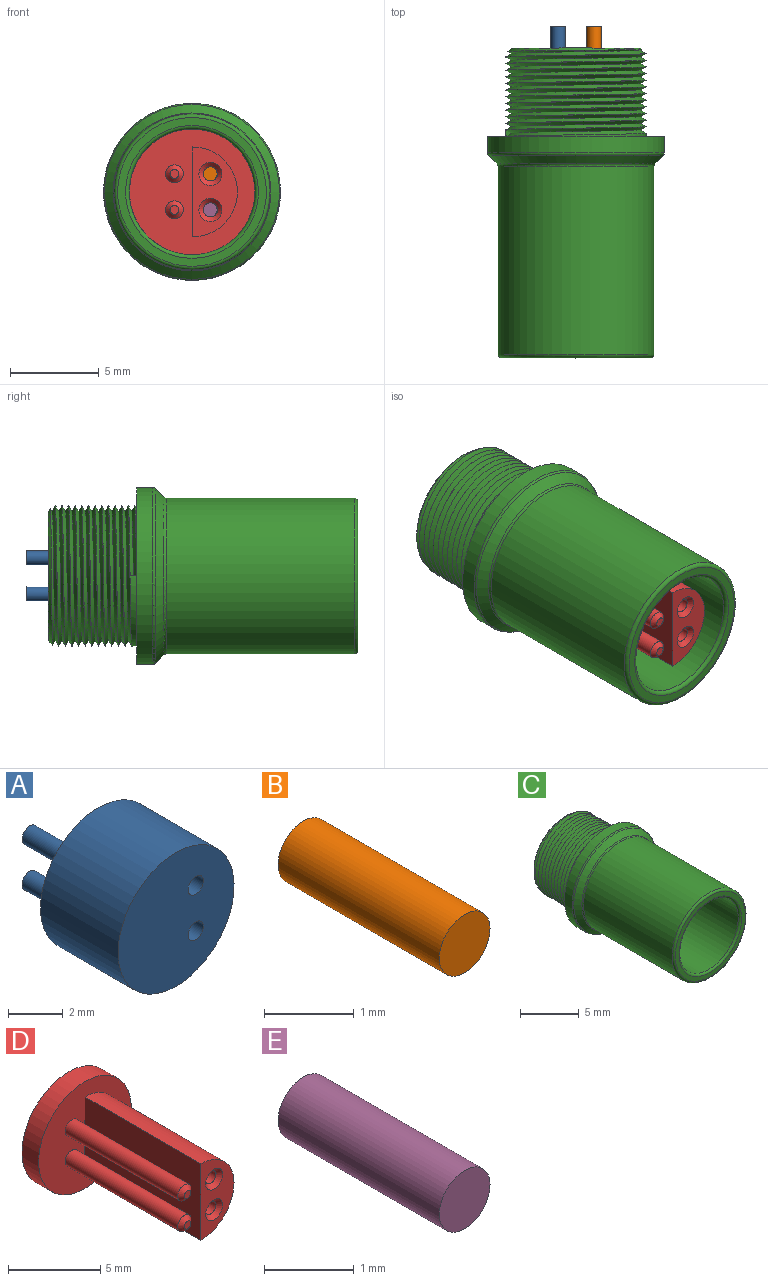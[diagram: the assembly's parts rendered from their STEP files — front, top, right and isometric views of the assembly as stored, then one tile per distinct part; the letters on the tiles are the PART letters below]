
ASSEMBLY  parts=5 mates=4
PART A: 13 faces, bbox 6x6.6x6 mm
  f0: cylinder r=3mm len=5.99mm, axis (0,1,0), area 75.6mm2, adj f1,f2
  f1: plane 5.99x5.99mm, normal (0,-1,0), area 27.2mm2, adj f0,f3,f4
  f2: plane 5.99x5.99mm, normal (0,1,0), area 26.2mm2, adj f0,f3,f4,f5,f7
  f3: cylinder r=0.4mm len=4.01mm, axis (0,-1,0), area 10.1mm2, adj f1,f2
  f4: cylinder r=0.4mm len=4.01mm, axis (0,-1,0), area 10.1mm2, adj f1,f2
  f5: cylinder r=0.4mm len=2.54mm, axis (0,-1,0), area 6.4mm2, adj f2,f6
  f6: plane 0.8x0.8mm, normal (0,1,0), area 0.2mm2, adj f5,f11
  f7: cylinder r=0.4mm len=2.54mm, axis (0,-1,0), area 6.4mm2, adj f2,f8
  f8: plane 0.8x0.8mm, normal (0,1,0), area 0.2mm2, adj f7,f9
  f9: cylinder r=0.32mm len=1.27mm, axis (0,1,0), area 2.5mm2, adj f8,f10
  f10: plane 0.64x0.64mm, normal (0,1,0), area 0.3mm2, adj f9
  f11: cylinder r=0.32mm len=1.27mm, axis (0,1,0), area 2.5mm2, adj f6,f12
  f12: plane 0.64x0.64mm, normal (0,1,0), area 0.3mm2, adj f11
PART B: 5 faces, bbox 0.8x2.5x0.8 mm
  f0: cylinder r=0.4mm len=2.54mm, axis (0,-1,0), area 6.4mm2, adj f1,f2
  f1: plane 0.8x0.8mm, normal (0,1,0), area 0.2mm2, adj f0,f3
  f2: plane 0.8x0.8mm, normal (0,-1,0), area 0.5mm2, adj f0
  f3: cylinder r=0.32mm len=1.27mm, axis (0,1,0), area 2.5mm2, adj f1,f4
  f4: plane 0.64x0.64mm, normal (0,1,0), area 0.3mm2, adj f3
PART C: 30 faces, bbox 10.8x17.8x10.8 mm
  f0: cylinder r=5mm len=10mm, axis (0,1,0), area 28.8mm2, adj f18,f22
  f1: cylinder r=4.4mm len=10.62mm, axis (0,-1,0), area 293.5mm2, adj f21,f29
  f2: plane 8.4x8.4mm, normal (0,-1,0), area 11.2mm2, adj f28,f29
  f3: cylinder r=3.55mm len=10.7mm, axis (0,-1,0), area 238.7mm2, adj f4,f28
  f4: plane 7.1x7.1mm, normal (0,-1,0), area 11.3mm2, adj f3,f27
  f5: cylinder r=3.96mm len=7.92mm, axis (0,1,0), area 4.8mm2, adj f6,f18,f23,f24,f25
  f6: cylinder r=3.96mm len=7.92mm, axis (0,1,0), area 0.1mm2, adj f5,f7,f23,f24
  f7: cylinder r=3.96mm len=7.92mm, axis (0,1,0), area 0.1mm2, adj f6,f8,f23,f24
  f8: cylinder r=3.96mm len=7.92mm, axis (0,1,0), area 0.1mm2, adj f7,f9,f23,f24
  f9: cylinder r=3.96mm len=7.92mm, axis (0,1,0), area 0.1mm2, adj f8,f10,f23,f24
  f10: cylinder r=3.96mm len=7.92mm, axis (0,1,0), area 0.1mm2, adj f9,f11,f23,f24
  f11: cylinder r=3.96mm len=7.92mm, axis (0,1,0), area 0.1mm2, adj f10,f12,f23,f24
  f12: cylinder r=3.96mm len=7.92mm, axis (0,1,0), area 0.1mm2, adj f11,f13,f23,f24
  f13: cylinder r=3.96mm len=7.92mm, axis (0,1,0), area 0.1mm2, adj f12,f14,f23,f24
  f14: cylinder r=3.96mm len=7.92mm, axis (0,1,0), area 0.1mm2, adj f13,f15,f23,f24
  f15: cylinder r=3.96mm len=7.92mm, axis (0,1,0), area 0.1mm2, adj f14,f16,f23,f24
  f16: cylinder r=3.96mm len=7.92mm, axis (0,1,0), area 0.1mm2, adj f15,f17,f23,f24
  f17: cylinder r=3.96mm len=4.98mm, axis (0,1,0), area 0mm2, adj f16,f23,f24,f26
  f18: plane 10x10mm, normal (0,1,0), area 29.2mm2, adj f0,f5
  f19: plane 7.33x7.33mm, normal (0,1,0), area 13.8mm2, adj f23,f24,f26,f27
  f20: cone r=4.4mm half-angle=45deg, axis (0,1,0), area 20.2mm2, adj f21,f22
  f21: torus R=4.6mm, axis (0,-1,0), area 4.4mm2, adj f1,f20
  f22: torus R=4.8mm, axis (0,-1,0), area 4.9mm2, adj f0,f20
  f23: bspline ~9.15x7.92mm, area 112.3mm2, adj f5,f6,f7,f8,f9,f10,f11,f12
  f24: bspline ~9.15x7.92mm, area 108mm2, adj f5,f6,f7,f8,f9,f10,f11,f12
  f25: plane 0.37x0.32mm, normal (0,0,1), area 0.1mm2, adj f5,f23,f24
  f26: cone r=3.66mm half-angle=45deg, axis (0,-1,0), area 4.8mm2, adj f17,f19,f23,f24
  f27: cylinder r=3mm len=6.6mm, axis (0,1,0), area 124.4mm2, adj f4,f19
  f28: torus R=3.75mm, axis (0,-1,0), area 7.2mm2, adj f2,f3
  f29: torus R=4.2mm, axis (0,-1,0), area 8.5mm2, adj f1,f2
PART D: 16 faces, bbox 7.1x10.2x7.1 mm
  f0: plane 7.11x7.11mm, normal (0,-1,0), area 28mm2, adj f1,f3,f4,f11,f13
  f1: cylinder r=3.56mm len=7.11mm, axis (0,1,0), area 28.4mm2, adj f0,f2
  f2: plane 7.11x7.11mm, normal (0,1,0), area 38.7mm2, adj f1,f6,f7
  f3: plane 8.89x5.08mm, normal (-1,0,0), area 45.2mm2, adj f0,f4,f5
  f4: cylinder r=2.54mm len=8.89mm, axis (0,1,0), area 70.9mm2, adj f0,f3,f5
  f5: plane 5.08x2.54mm, normal (0,-1,0), area 7.5mm2, adj f3,f4,f8,f9
  f6: cylinder r=0.4mm len=9.91mm, axis (0,-1,0), area 24.8mm2, adj f2,f8
  f7: cylinder r=0.4mm len=9.91mm, axis (0,-1,0), area 24.8mm2, adj f2,f9
  f8: cone r=0.4mm half-angle=45deg, axis (0,-1,0), area 1.2mm2, adj f5,f6
  f9: cone r=0.4mm half-angle=45deg, axis (0,-1,0), area 1.2mm2, adj f5,f7
  f10: plane 0.51x0.51mm, normal (0,-1,0), area 0.2mm2, adj f15
  f11: cylinder r=0.51mm len=8.64mm, axis (0,1,0), area 27.6mm2, adj f0,f15
  f12: plane 0.51x0.51mm, normal (0,-1,0), area 0.2mm2, adj f14
  f13: cylinder r=0.51mm len=8.64mm, axis (0,1,0), area 27.6mm2, adj f0,f14
  f14: cone r=0.25mm half-angle=45deg, axis (0,1,0), area 0.9mm2, adj f12,f13
  f15: cone r=0.25mm half-angle=45deg, axis (0,1,0), area 0.9mm2, adj f10,f11
PART E: 5 faces, bbox 0.8x2.5x0.8 mm
  f0: cylinder r=0.4mm len=2.54mm, axis (0,-1,0), area 6.4mm2, adj f1,f2
  f1: plane 0.8x0.8mm, normal (0,1,0), area 0.2mm2, adj f0,f3
  f2: plane 0.8x0.8mm, normal (0,-1,0), area 0.5mm2, adj f0
  f3: cylinder r=0.32mm len=1.27mm, axis (0,1,0), area 2.5mm2, adj f1,f4
  f4: plane 0.64x0.64mm, normal (0,1,0), area 0.3mm2, adj f3
PLACE A t=(3.98,7.58,-3.09)mm
PLACE B t=(3.98,7.58,-3.09)mm
PLACE C t=(3.98,8.87,-3.09)mm
PLACE D t=(4.01,6.29,-3.09)mm
PLACE E t=(3.98,7.58,-3.09)mm
MATE pin_slot E.f0 <-> A.f3  axis (0,-1,0) through (5,7.58,-4.11)mm
MATE slider D.f2 <-> C.f0  axis (0,1,0) through (3.98,2.27,-3.09)mm
MATE slider B.f0 <-> A.f4  axis (0,-1,0) through (5,7.58,-2.08)mm
MATE slider A.f0 <-> C.f27  axis (0,1,0) through (3.98,5.57,-3.09)mm
